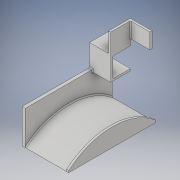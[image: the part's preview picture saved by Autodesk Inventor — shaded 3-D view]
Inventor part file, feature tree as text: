
AUTODESK INVENTOR PART (.ipt)
format: ipt  version: 2017 (Build 210142000, 142)  size: 225,792 bytes
history: native  units: in
note: dims shown in document units (in); Inventor stores cm internally (conversion verified against a paired STEP export)
features: extrude x7, sketch x7, projected_geometry x7, fillet x1
ambient origin geometry x8: Origin, YZ Plane, XZ Plane, XY Plane, X Axis, Y Axis, Z Axis, Center Point
bodies: Solid1 (feature_tree)
feature tree (22):
  extrude  "Extrusion1"  Depth=0.0787in
  extrude  "Extrusion2"  Depth=0.7283in
  extrude  "Extrusion3"  Depth=0.7283in
  extrude  "Extrusion4"  Depth=0.2362in
  extrude  "Extrusion5"  Depth=0.7283in TaperAngle=0.0deg
  extrude  "Extrusion6"  Depth=1.1811in
  extrude  "Extrusion7"  Depth=0.0394in
  fillet  "Fillet1"  Radius=1.5354in
  sketch  "Sketch1"  dims[d0=0.7283in d1=0.0787in]
  sketch  "Sketch2"  dims[d2=0.0787in d3=0.7283in]
  projected_geometry  "Projected Loop1"
  sketch  "Sketch3"  dims[d4=0.7874in d5=0.0in d6=0.7283in]
  projected_geometry  "Projected Loop2"
  sketch  "Sketch4"  dims[d7=0.0787in d8=0.0in d9=0.2362in]
  projected_geometry  "Projected Loop3"
  sketch  "Sketch5"  dims[d10=0.0787in d11=0.7283in d12=0.0787in d13=0.0in d14=0.0in]
  projected_geometry  "Projected Loop4"
  sketch  "Sketch7"  dims[d15=3.2283in d16=1.1811in]
  projected_geometry  "Projected Loop6"
  sketch  "Sketch8"  dims[d17=0.1181in d18=0.0in d20=0.5906in d21=1.5354in d22=0.0in d33=0.0787in d34=0.0787in d35=0.0787in d36=0.0787in d37=0.0in d38=0.0787in d39=0.0in d40=0.0394in]
  projected_geometry  "Projected Loop7"
  projected_geometry  "Projected Loop8"
